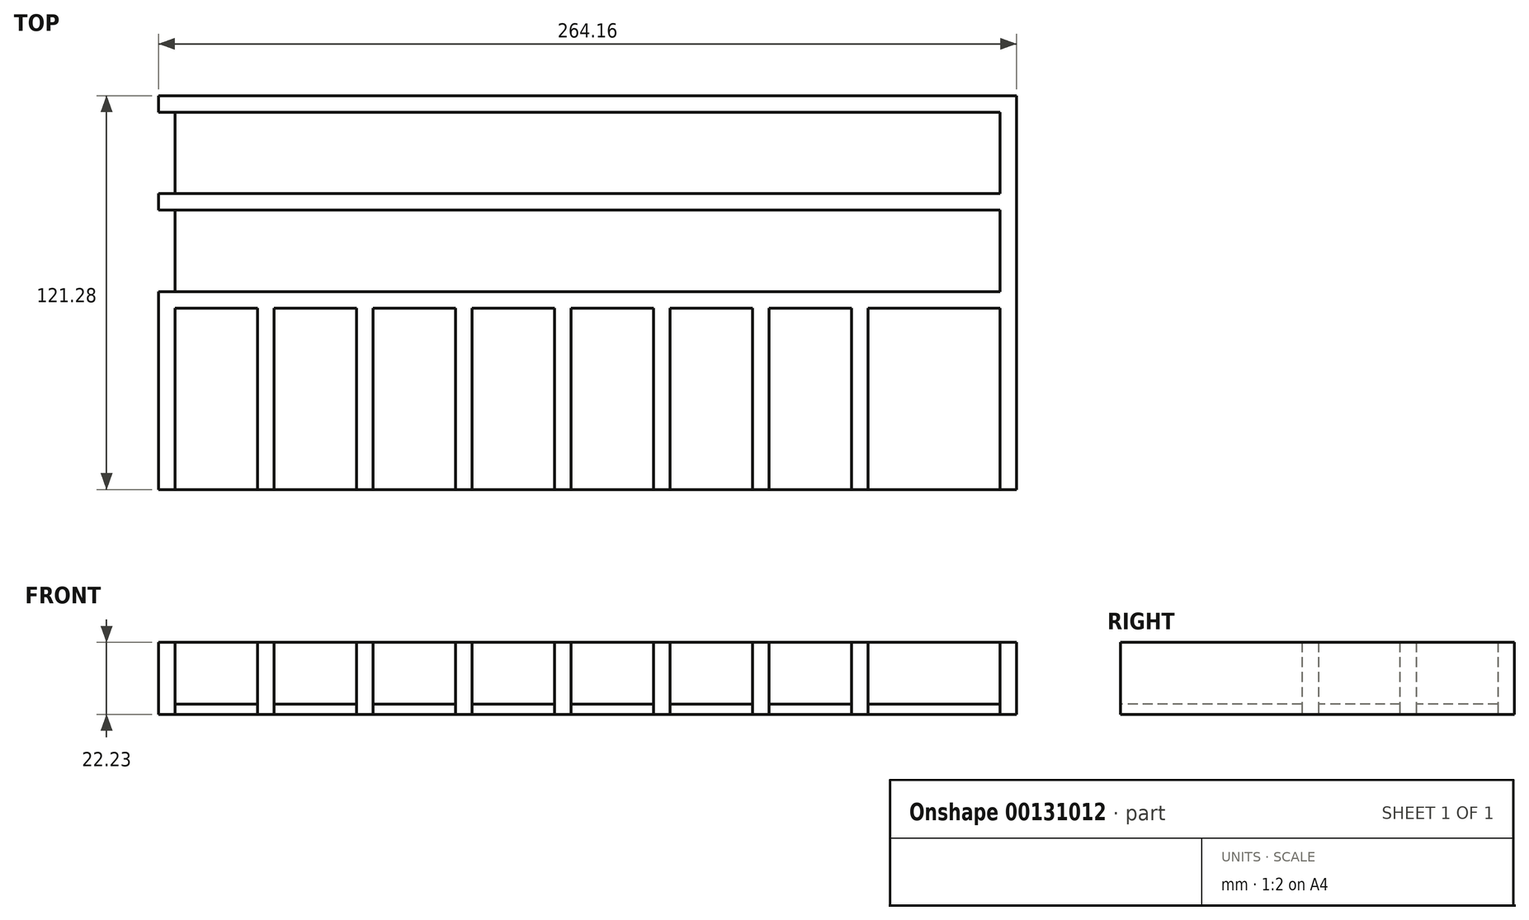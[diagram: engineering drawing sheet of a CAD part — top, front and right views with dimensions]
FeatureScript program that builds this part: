
annotation { "Feature Type Name" : "Feature", "Feature Type Description" : "" }
export const myFeature = defineFeature(function(context is Context, id is Id, definition is map)
    precondition{}
    {
        {
            var Q0;
            Q0=qCreatedBy(makeId("Top.planeOp"),FACE);
            var sketch = newSketch(context, id + "F0", { "sketchPlane" : qUnion([Q0])});
            skLineSegment(sketch, "E0.bottom", {"start": v(-142.59, 55.17) * mm, "end": v(121.57, 55.17) * mm});
            skLineSegment(sketch, "E0.top", {"start": v(-142.59, -66.11) * mm, "end": v(121.57, -66.11) * mm});
            skLineSegment(sketch, "E0.left", {"start": v(-142.59, 55.17) * mm, "end": v(-142.59, -66.11) * mm});
            skLineSegment(sketch, "E0.right", {"start": v(121.57, 55.17) * mm, "end": v(121.57, -66.11) * mm});
            skLineSegment(sketch, "E1.0", {"start": v(-137.5, 50.1) * mm, "end": v(116.5, 50.1) * mm});
            skPoint(sketch, "E2", {"position": v(-137.5, -10.23) * mm});
            skLineSegment(sketch, "E3", {"start": v(-137.5, -10.23) * mm, "end": v(116.5, -10.23) * mm});
            skLineSegment(sketch, "E4.0", {"start": v(-137.5, -5.15) * mm, "end": v(116.5, -5.15) * mm});
            skPoint(sketch, "E5", {"position": v(-137.5, 19.93) * mm});
            skLineSegment(sketch, "E6", {"start": v(-137.5, 19.93) * mm, "end": v(116.5, 19.93) * mm});
            skLineSegment(sketch, "E7.0", {"start": v(-137.5, 25.01) * mm, "end": v(116.5, 25.01) * mm});
            skLineSegment(sketch, "E8", {"start": v(-137.5, 50.1) * mm, "end": v(-137.5, 25.01) * mm});
            skLineSegment(sketch, "E9", {"start": v(-137.5, -10.23) * mm, "end": v(-137.5, -61.03) * mm});
            skPoint(sketch, "E10", {"position": v(-142.59, 50.1) * mm});
            skPoint(sketch, "E11", {"position": v(-142.59, 25.01) * mm});
            skPoint(sketch, "E12", {"position": v(-142.59, 19.93) * mm});
            skPoint(sketch, "E13", {"position": v(-142.59, -5.15) * mm});
            skPoint(sketch, "E14", {"position": v(-142.59, -10.23) * mm});
            skPoint(sketch, "E15", {"position": v(-142.59, -61.03) * mm});
            skLineSegment(sketch, "E16", {"start": v(-137.5, 19.93) * mm, "end": v(-137.5, -5.15) * mm});
            skLineSegment(sketch, "E17", {"start": v(116.5, -10.23) * mm, "end": v(116.5, -61.03) * mm});
            skLineSegment(sketch, "E18", {"start": v(116.5, -5.15) * mm, "end": v(116.5, 19.93) * mm});
            skLineSegment(sketch, "E19", {"start": v(116.5, 25.01) * mm, "end": v(116.5, 50.1) * mm});
            skLineSegment(sketch, "E20", {"start": v(-112.1, -10.23) * mm, "end": v(-112.1, -61.03) * mm});
            skLineSegment(sketch, "E21", {"start": v(-107.03, -10.23) * mm, "end": v(-107.03, -61.03) * mm});
            skLineSegment(sketch, "E22", {"start": v(-81.63, -10.23) * mm, "end": v(-81.63, -61.03) * mm});
            skLineSegment(sketch, "E23", {"start": v(-76.55, -10.23) * mm, "end": v(-76.55, -61.03) * mm});
            skLineSegment(sketch, "E24", {"start": v(-51.15, -10.23) * mm, "end": v(-51.15, -61.03) * mm});
            skLineSegment(sketch, "E25", {"start": v(-46.07, -10.23) * mm, "end": v(-46.07, -61.03) * mm});
            skLineSegment(sketch, "E26", {"start": v(-20.67, -10.23) * mm, "end": v(-20.67, -61.03) * mm});
            skLineSegment(sketch, "E27", {"start": v(-15.59, -10.23) * mm, "end": v(-15.59, -61.03) * mm});
            skLineSegment(sketch, "E28", {"start": v(9.81, -10.23) * mm, "end": v(9.81, -61.03) * mm});
            skLineSegment(sketch, "E29", {"start": v(14.9, -10.23) * mm, "end": v(14.9, -61.03) * mm});
            skLineSegment(sketch, "E30", {"start": v(40.3, -10.23) * mm, "end": v(40.3, -61.03) * mm});
            skLineSegment(sketch, "E31", {"start": v(45.37, -10.23) * mm, "end": v(45.37, -61.03) * mm});
            skLineSegment(sketch, "E32", {"start": v(70.77, -10.23) * mm, "end": v(70.77, -61.03) * mm});
            skLineSegment(sketch, "E33", {"start": v(75.85, -10.23) * mm, "end": v(75.85, -61.03) * mm});
            skLineSegment(sketch, "E34", {"start": v(-137.5, -61.03) * mm, "end": v(-137.5, -66.11) * mm});
            skLineSegment(sketch, "E35", {"start": v(116.5, -61.03) * mm, "end": v(116.5, -66.11) * mm});
            skLineSegment(sketch, "E36", {"start": v(-112.1, -61.03) * mm, "end": v(-112.1, -66.11) * mm});
            skLineSegment(sketch, "E37", {"start": v(-107.03, -61.03) * mm, "end": v(-107.03, -66.11) * mm});
            skLineSegment(sketch, "E38", {"start": v(-81.63, -61.03) * mm, "end": v(-81.63, -66.11) * mm});
            skLineSegment(sketch, "E39", {"start": v(-76.55, -61.03) * mm, "end": v(-76.55, -66.11) * mm});
            skLineSegment(sketch, "E40", {"start": v(-51.15, -61.03) * mm, "end": v(-51.15, -66.11) * mm});
            skLineSegment(sketch, "E41", {"start": v(-46.07, -61.03) * mm, "end": v(-46.07, -66.11) * mm});
            skLineSegment(sketch, "E42", {"start": v(-20.67, -61.03) * mm, "end": v(-20.67, -66.11) * mm});
            skLineSegment(sketch, "E43", {"start": v(-15.59, -61.03) * mm, "end": v(-15.59, -66.11) * mm});
            skLineSegment(sketch, "E44", {"start": v(9.81, -61.03) * mm, "end": v(9.81, -66.11) * mm});
            skLineSegment(sketch, "E45", {"start": v(14.9, -61.03) * mm, "end": v(14.9, -66.11) * mm});
            skLineSegment(sketch, "E46", {"start": v(40.3, -61.03) * mm, "end": v(40.3, -66.11) * mm});
            skLineSegment(sketch, "E47", {"start": v(45.37, -61.03) * mm, "end": v(45.37, -66.11) * mm});
            skLineSegment(sketch, "E48", {"start": v(70.77, -61.03) * mm, "end": v(70.77, -66.11) * mm});
            skLineSegment(sketch, "E49", {"start": v(75.85, -61.03) * mm, "end": v(75.85, -66.11) * mm});
            skSolve(sketch);
        }
        {
            var Q0;
            Q0=makeQuery(id+"F0.imprint","IMPRINT",FACE,{"disambiguationData":[TD([[makeQuery(id+"F0.imprint","IMPRINT",EDGE,{"derivedFrom":sQuery(id+"F0.wireOp",EDGE,"E1.0")}),-1.0]])]});
            var Q1;
            Q1=makeQuery(id+"F0.imprint","IMPRINT",FACE,{"disambiguationData":[TD([[makeQuery(id+"F0.imprint","IMPRINT",EDGE,{"derivedFrom":sQuery(id+"F0.wireOp",EDGE,"E4.0")}),1.0]])]});
            var Q2;
            Q2=makeQuery(id+"F0.imprint","IMPRINT",FACE,{"disambiguationData":[TD([[makeQuery(id+"F0.imprint","IMPRINT",EDGE,{"derivedFrom":sQuery(id+"F0.wireOp",EDGE,"E1.2")}),1.0]])]});
            var Q3;
            {var subQ1=sQuery(id+"F0.wireOp",EDGE,"E9");Q3=makeQuery(id+"F0.imprint","IMPRINT",FACE,{"disambiguationData":[TD([[makeQuery(id+"F0.imprint","IMPRINT",EDGE,{"derivedFrom":subQ1}),1.0]])]});}
            var Q4;
            {var subQ1=sQuery(id+"F0.wireOp",EDGE,"E21");Q4=makeQuery(id+"F0.imprint","IMPRINT",FACE,{"disambiguationData":[TD([[makeQuery(id+"F0.imprint","IMPRINT",EDGE,{"derivedFrom":subQ1}),1.0]])]});}
            var Q5;
            {var subQ0=sQuery(id+"F0.wireOp",EDGE,"E23");Q5=makeQuery(id+"F0.imprint","IMPRINT",FACE,{"disambiguationData":[TD([[makeQuery(id+"F0.imprint","IMPRINT",EDGE,{"derivedFrom":subQ0}),1.0]])]});}
            var Q6;
            {var subQ1=sQuery(id+"F0.wireOp",EDGE,"E25");Q6=makeQuery(id+"F0.imprint","IMPRINT",FACE,{"disambiguationData":[TD([[makeQuery(id+"F0.imprint","IMPRINT",EDGE,{"derivedFrom":subQ1}),1.0]])]});}
            var Q7;
            {var subQ1=sQuery(id+"F0.wireOp",EDGE,"E27");Q7=makeQuery(id+"F0.imprint","IMPRINT",FACE,{"disambiguationData":[TD([[makeQuery(id+"F0.imprint","IMPRINT",EDGE,{"derivedFrom":subQ1}),1.0]])]});}
            var Q8;
            {var subQ1=sQuery(id+"F0.wireOp",EDGE,"E29");Q8=makeQuery(id+"F0.imprint","IMPRINT",FACE,{"disambiguationData":[TD([[makeQuery(id+"F0.imprint","IMPRINT",EDGE,{"derivedFrom":subQ1}),1.0]])]});}
            var Q9;
            {var subQ0=sQuery(id+"F0.wireOp",EDGE,"E31");Q9=makeQuery(id+"F0.imprint","IMPRINT",FACE,{"disambiguationData":[TD([[makeQuery(id+"F0.imprint","IMPRINT",EDGE,{"derivedFrom":subQ0}),1.0]])]});}
            var Q10;
            {var subQ1=sQuery(id+"F0.wireOp",EDGE,"E17");Q10=makeQuery(id+"F0.imprint","IMPRINT",FACE,{"disambiguationData":[TD([[makeQuery(id+"F0.imprint","IMPRINT",EDGE,{"derivedFrom":subQ1}),-1.0]])]});}
            extrude(context, id + "F1", {"entities" : qUnion([Q0, Q1, Q2, Q3, Q4, Q5, Q6, Q7, Q8, Q9, Q10]), "depth" : 3.17 * mm});
        }
        {
            var Q0;
            Q0=makeQuery(id+"F0.imprint","IMPRINT",FACE,{"disambiguationData":[TD([[makeQuery(id+"F0.imprint","IMPRINT",EDGE,{"derivedFrom":sQuery(id+"F0.wireOp",EDGE,"E0.bottom")}),-1.0]])]});
            var Q1;
            {var subQ1=sQuery(id+"F0.wireOp",EDGE,"E20");Q1=makeQuery(id+"F0.imprint","IMPRINT",FACE,{"disambiguationData":[TD([[makeQuery(id+"F0.imprint","IMPRINT",EDGE,{"derivedFrom":subQ1}),1.0]])]});}
            var Q2;
            {var subQ1=sQuery(id+"F0.wireOp",EDGE,"E22");Q2=makeQuery(id+"F0.imprint","IMPRINT",FACE,{"disambiguationData":[TD([[makeQuery(id+"F0.imprint","IMPRINT",EDGE,{"derivedFrom":subQ1}),1.0]])]});}
            var Q3;
            {var subQ0=sQuery(id+"F0.wireOp",EDGE,"E24");Q3=makeQuery(id+"F0.imprint","IMPRINT",FACE,{"disambiguationData":[TD([[makeQuery(id+"F0.imprint","IMPRINT",EDGE,{"derivedFrom":subQ0}),1.0]])]});}
            var Q4;
            {var subQ1=sQuery(id+"F0.wireOp",EDGE,"E26");Q4=makeQuery(id+"F0.imprint","IMPRINT",FACE,{"disambiguationData":[TD([[makeQuery(id+"F0.imprint","IMPRINT",EDGE,{"derivedFrom":subQ1}),1.0]])]});}
            var Q5;
            {var subQ1=sQuery(id+"F0.wireOp",EDGE,"E28");Q5=makeQuery(id+"F0.imprint","IMPRINT",FACE,{"disambiguationData":[TD([[makeQuery(id+"F0.imprint","IMPRINT",EDGE,{"derivedFrom":subQ1}),1.0]])]});}
            var Q6;
            {var subQ1=sQuery(id+"F0.wireOp",EDGE,"E30");Q6=makeQuery(id+"F0.imprint","IMPRINT",FACE,{"disambiguationData":[TD([[makeQuery(id+"F0.imprint","IMPRINT",EDGE,{"derivedFrom":subQ1}),1.0]])]});}
            var Q7;
            {var subQ0=sQuery(id+"F0.wireOp",EDGE,"E32");Q7=makeQuery(id+"F0.imprint","IMPRINT",FACE,{"disambiguationData":[TD([[makeQuery(id+"F0.imprint","IMPRINT",EDGE,{"derivedFrom":subQ0}),1.0]])]});}
            extrude(context, id + "F2", {"entities" : qUnion([Q0, Q1, Q2, Q3, Q4, Q5, Q6, Q7]), "depth" : 22.22 * mm});
        }
        {
            var Q0;
            Q0=makeQuery(id+"F2.opExtrude","SWEPT_FACE",FACE,{"disambiguationData":[OSD([sQuery(id+"F0.wireOp",EDGE,"E16")])]});
            var Q1;
            Q1=makeQuery(id+"F2.opExtrude","SWEPT_FACE",FACE,{"disambiguationData":[OSD([sQuery(id+"F0.wireOp",EDGE,"E8")])]});
            extrude(context, id + "F3", {"entities" : qUnion([Q0, Q1]), "operationType" : NewBodyOperationType.REMOVE, "oppositeDirection" : true, "depth" : 25.4 * mm});
        }
    });
